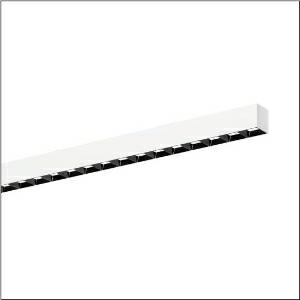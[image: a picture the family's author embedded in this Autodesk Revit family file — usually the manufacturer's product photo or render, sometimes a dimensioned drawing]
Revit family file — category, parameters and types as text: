
# Revit family: silica_21_51mx22dc4awb
name_source: partatom
category: Lighting Fixtures
units: mm (PartAtom-declared; Revit-internal decimal feet)

## family parameters
Cut with Voids When Loaded = No
Host = Face
Light Source = No
Part Type = Normal
Room Calculation Point = No
Round Connector Dimension = Use Diameter
Shared = No

## types (1)
- --- (1 x LED, 10800 lm, 64.7 W, 4000K)
    Apparent Load = 65 VA
    CIE Flux Codes = 86 100 100 100 100
    Color Rendering = 80
    Color Temperature = 4000K
    Default Elevation = 1800 mm
    Description = Silica 21, office luminaire, primary light control with darklight reflector, of PMMA, black, CAT 2 (L<= 3000cd/m²), light emission: direct distribution, primary light characteristic: symmetric, installation type: surface-mounted, LED, rated luminous flux: 10.800lm, luminous efficacy: 167lm/W, light colour: 840, colour temperature: 4000K, control gear: DALI 2, with terminal, 3+2-pole, max. 2.5mm², mains connection: 220..240V, AC, 50/60Hz, rated input power: 64.7W, luminaire housing, of aluminium, traffic white (RAL 9016), length: 3.004mm, width: 53mm, height: 53mm, protection rating (complete): IP20, insulation class (complete): insulation class I (protective earthing), certification: CE, permissible operating ambient temperature: 0..+35°C, standard: EN 50419, packaging unit: 1 piece
    Height = 53 mm
    Lamp = 1 x LED
    Lamp Light Flux = 10800 lm
    Lamp Power = 64.7 W
    Lamp count = 1
    Length = 3004 mm
    Luminous efficacy = 167 lm/W
    Manufacturer = Siteco
    ModVariant = No
    Model = 51MX22DC4AWB
    Mounting Place = Ceiling
    Mounting Type = Surface mounted
    Number of Poles = 1
    OnlyDefault = Yes
    Power Factor = 1
    Product Name = Silica 21
    Product group = office luminaire | ceiling mounted
    ProductGroupID = 301
    Protection Class = Protection class I
    Protection Degree = IP 20
    RLX_Detail_Level = 1
    RLX_Emergency_Light_Flux = 0 lm
    RLX_Emergency_Type = 0
    RLX_Emergency_Type_DB = No
    RlxData = <blob elided: 61521 chars, md5=9198f44f>
    Socket = socket
    Standby Power = 0 W
    System Light Flux = 10800 lm
    System Power = 65 W
    Type Comments = factory setting: luminous flux: 100 % | dim-lin: 254 | 366 mA
    Type Image = l_1335873.jpg
    URL = http://relux.com
    VarID = @adj_125049
    Voltage = 0 V
    Weight = 0.00 kg
    Width = 53 mm

## geometry (parser evidence)
native form markers: Blend x4, Sweep x12
no freeform markers — native parametric forms only
